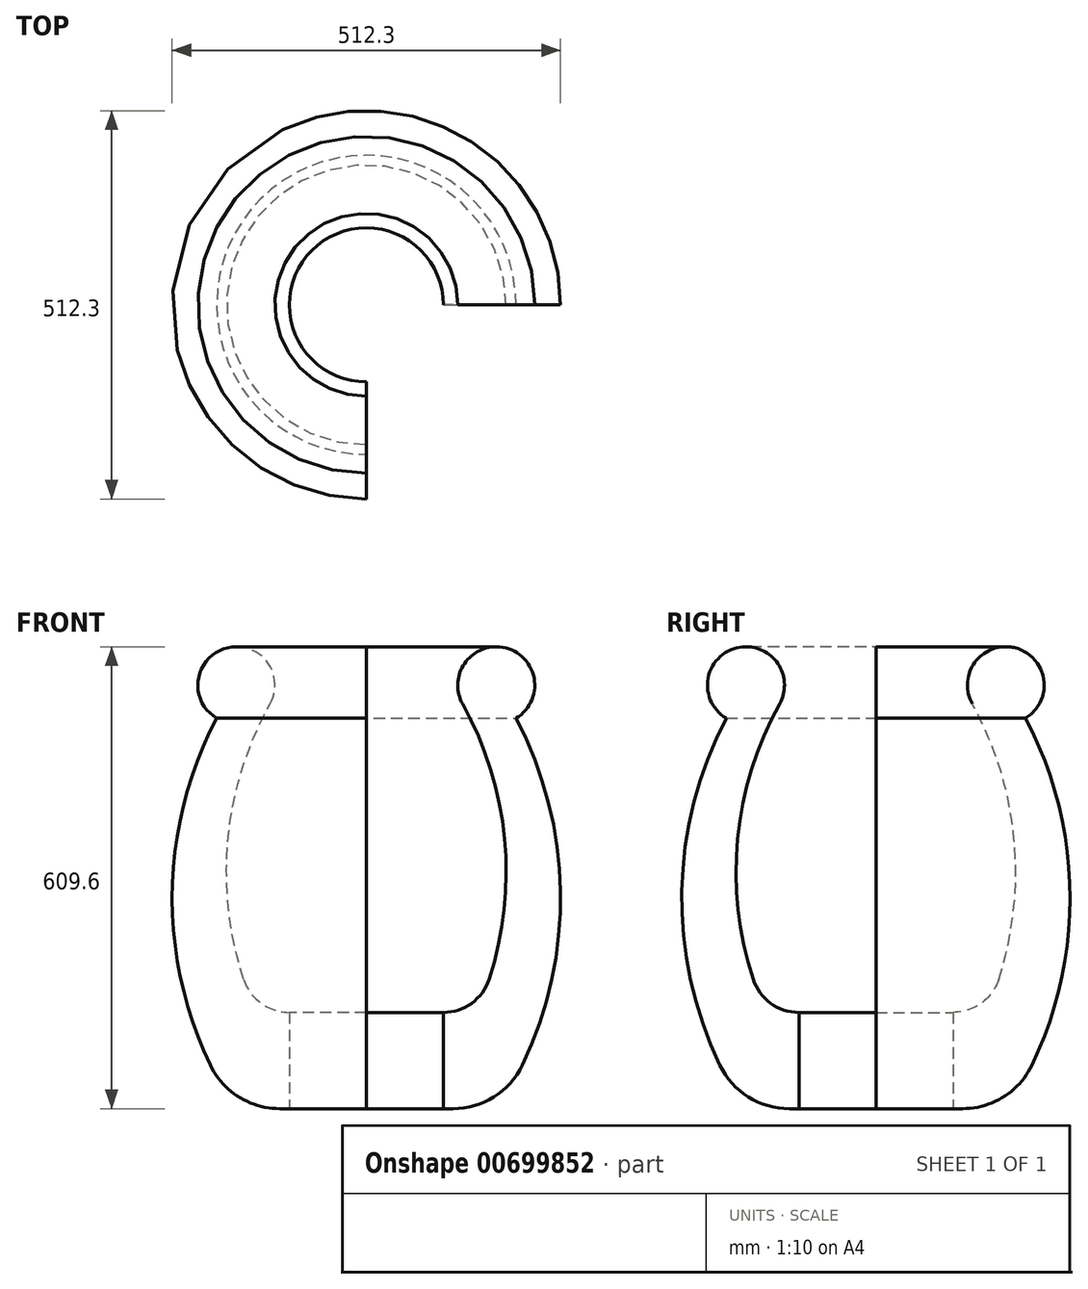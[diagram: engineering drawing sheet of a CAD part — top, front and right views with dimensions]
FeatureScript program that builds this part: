
annotation { "Feature Type Name" : "Feature", "Feature Type Description" : "" }
export const myFeature = defineFeature(function(context is Context, id is Id, definition is map)
    precondition{}
    {
        {
            var Q0;
            Q0=qCreatedBy(makeId("Front.planeOp"),FACE);
            var sketch = newSketch(context, id + "F0", { "sketchPlane" : qUnion([Q0])});
            skLineSegment(sketch, "E0", {"start": v(0, 0) * mm, "end": v(0, 719.83) * mm, "construction": true});
            skLineSegment(sketch, "E1", {"start": v(114.3, 78.95) * mm, "end": v(114.3, 0) * mm});
            skLineSegment(sketch, "E2", {"start": v(381, 727.2) * mm, "end": v(381, -112.59) * mm, "construction": true});
            skLineSegment(sketch, "E3", {"start": v(-124.84, 645.16) * mm, "end": v(765.44, 645.16) * mm});
            skLineSegment(sketch, "E4", {"start": v(114.3, 78.95) * mm, "end": v(114.3, 714.98) * mm, "construction": true});
            skArc(sketch, "E5", {"start": v(101.6, 127) * mm, "mid": v(138.91, 139.12) * mm, "end": v(161.98, 170.85) * mm});
            skArc(sketch, "E6", {"start": v(161.98, 170.85) * mm, "mid": v(182.33, 356.14) * mm, "end": v(127.03, 534.16) * mm});
            skArc(sketch, "E7", {"start": v(205.84, 57.51) * mm, "mid": v(256.06, 287.32) * mm, "end": v(197.38, 515.12) * mm});
            skArc(sketch, "E8.trimOffspring", {"start": v(114.3, 0) * mm, "mid": v(168.35, 15.57) * mm, "end": v(205.84, 57.51) * mm});
            skLineSegment(sketch, "E9", {"start": v(120.65, 406.95) * mm, "end": v(120.65, 550.02) * mm, "construction": true});
            skArc(sketch, "E10", {"start": v(197.38, 515.12) * mm, "mid": v(184.72, 607.84) * mm, "end": v(127.03, 534.16) * mm});
            skLineSegment(sketch, "E11", {"start": v(114.3, 0) * mm, "end": v(514.86, 0) * mm, "construction": true});
            skLineSegment(sketch, "E12", {"start": v(101.6, 127) * mm, "end": v(101.6, 0) * mm});
            skLineSegment(sketch, "E13", {"start": v(114.3, 0) * mm, "end": v(101.6, 0) * mm});
            skLineSegment(sketch, "E14", {"start": v(-153.27, 177.8) * mm, "end": v(640.71, 177.8) * mm, "construction": true});
            skArc(sketch, "E15", {"start": v(197.38, 515.12) * mm, "mid": v(184.96, 537.28) * mm, "end": v(171.45, 558.8) * mm, "construction": true});
            skSolve(sketch);
        }
        {
            var Q0;
            Q0=makeQuery(id+"F0.imprint","IMPRINT",FACE,{"disambiguationData":[TD([[makeQuery(id+"F0.imprint","IMPRINT",EDGE,{"derivedFrom":sQuery(id+"F0.wireOp",EDGE,"E5")}),-1.0]])]});
            var Q1;
            Q1=sQuery(id+"F0.wireOp",EDGE,"E0");
            revolve(context, id + "F1", {"surfaceOperationType" : NewSurfaceOperationType.NEW, "entities" : qUnion([Q0]), "axis" : qUnion([Q1]), "revolveType" : RevolveType.ONE_DIRECTION, "angle" : 270 * degree});
        }
    });
